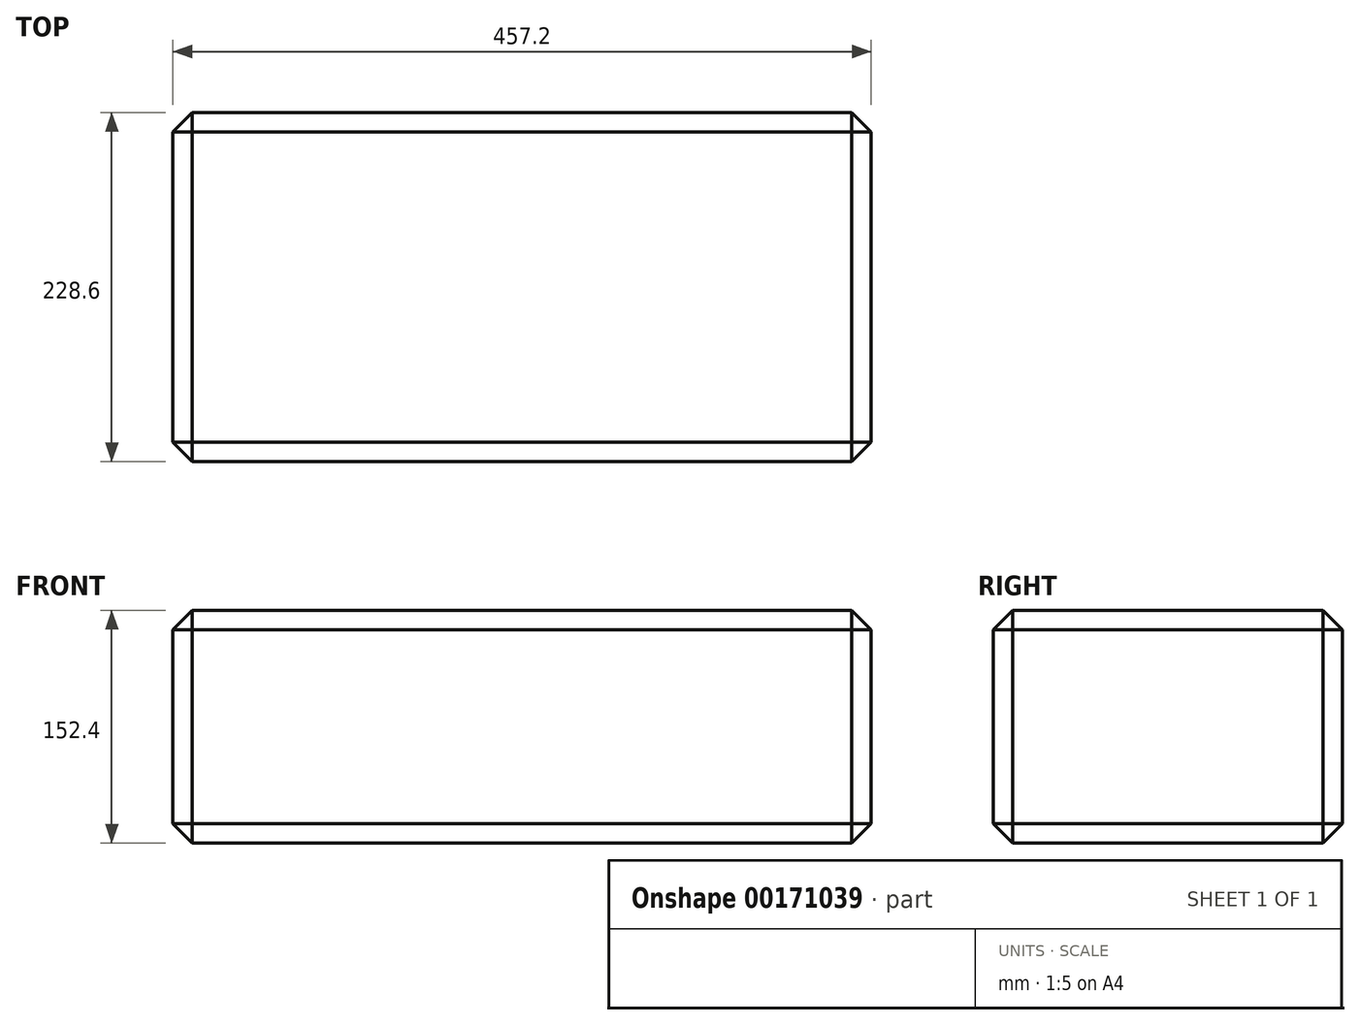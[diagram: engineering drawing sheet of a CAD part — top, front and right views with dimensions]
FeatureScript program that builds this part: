
annotation { "Feature Type Name" : "Feature", "Feature Type Description" : "" }
export const myFeature = defineFeature(function(context is Context, id is Id, definition is map)
    precondition{}
    {
        {
            var Q0;
            Q0=qCreatedBy(makeId("Top.planeOp"),FACE);
            var sketch = newSketch(context, id + "F0", { "sketchPlane" : qUnion([Q0])});
            skLineSegment(sketch, "E0.bottom", {"start": v(-228.6, 114.3) * mm, "end": v(228.6, 114.3) * mm});
            skLineSegment(sketch, "E0.top", {"start": v(-228.6, -114.3) * mm, "end": v(228.6, -114.3) * mm});
            skLineSegment(sketch, "E0.left", {"start": v(-228.6, 114.3) * mm, "end": v(-228.6, -114.3) * mm});
            skLineSegment(sketch, "E0.right", {"start": v(228.6, 114.3) * mm, "end": v(228.6, -114.3) * mm});
            skLineSegment(sketch, "E1", {"start": v(0, 0) * mm, "end": v(0, 114.3) * mm, "construction": true});
            skLineSegment(sketch, "E2", {"start": v(-228.6, 0) * mm, "end": v(0, 0) * mm, "construction": true});
            skSolve(sketch);
        }
        {
            var Q0;
            Q0=makeQuery(id+"F0.imprint","IMPRINT",FACE,{"disambiguationData":[TD([[makeQuery(id+"F0.imprint","IMPRINT",EDGE,{"derivedFrom":sQuery(id+"F0.wireOp",EDGE,"E0.bottom")}),-1.0]])]});
            extrude(context, id + "F1", {"entities" : qUnion([Q0]), "depth" : 152.4 * mm});
        }
        {
            var Q0;
            Q0=makeQuery(id+"F1.opExtrude","CAP_FACE",FACE,{"disambiguationData":[OSD([sQuery(id+"F0.wireOp",EDGE,"E0.bottom"),sQuery(id+"F0.wireOp",EDGE,"E0.top"),sQuery(id+"F0.wireOp",EDGE,"E0.left"),sQuery(id+"F0.wireOp",EDGE,"E0.right")])],"isStart":false});
            var Q1;
            Q1=makeQuery(id+"F1.opExtrude","CAP_FACE",FACE,{"disambiguationData":[OSD([sQuery(id+"F0.wireOp",EDGE,"E0.bottom"),sQuery(id+"F0.wireOp",EDGE,"E0.top"),sQuery(id+"F0.wireOp",EDGE,"E0.left"),sQuery(id+"F0.wireOp",EDGE,"E0.right")])],"isStart":true});
            var Q2;
            Q2=makeQuery(id+"F1.opExtrude","SWEPT_FACE",FACE,{"disambiguationData":[OSD([sQuery(id+"F0.wireOp",EDGE,"E0.left")])]});
            var Q3;
            Q3=makeQuery(id+"F1.opExtrude","SWEPT_FACE",FACE,{"disambiguationData":[OSD([sQuery(id+"F0.wireOp",EDGE,"E0.right")])]});
            chamfer(context, id + "F2", {"entities" : qUnion([Q0, Q1, Q2, Q3]), "width" : 12.7 * mm, "tangentPropagation" : true});
        }
    });
